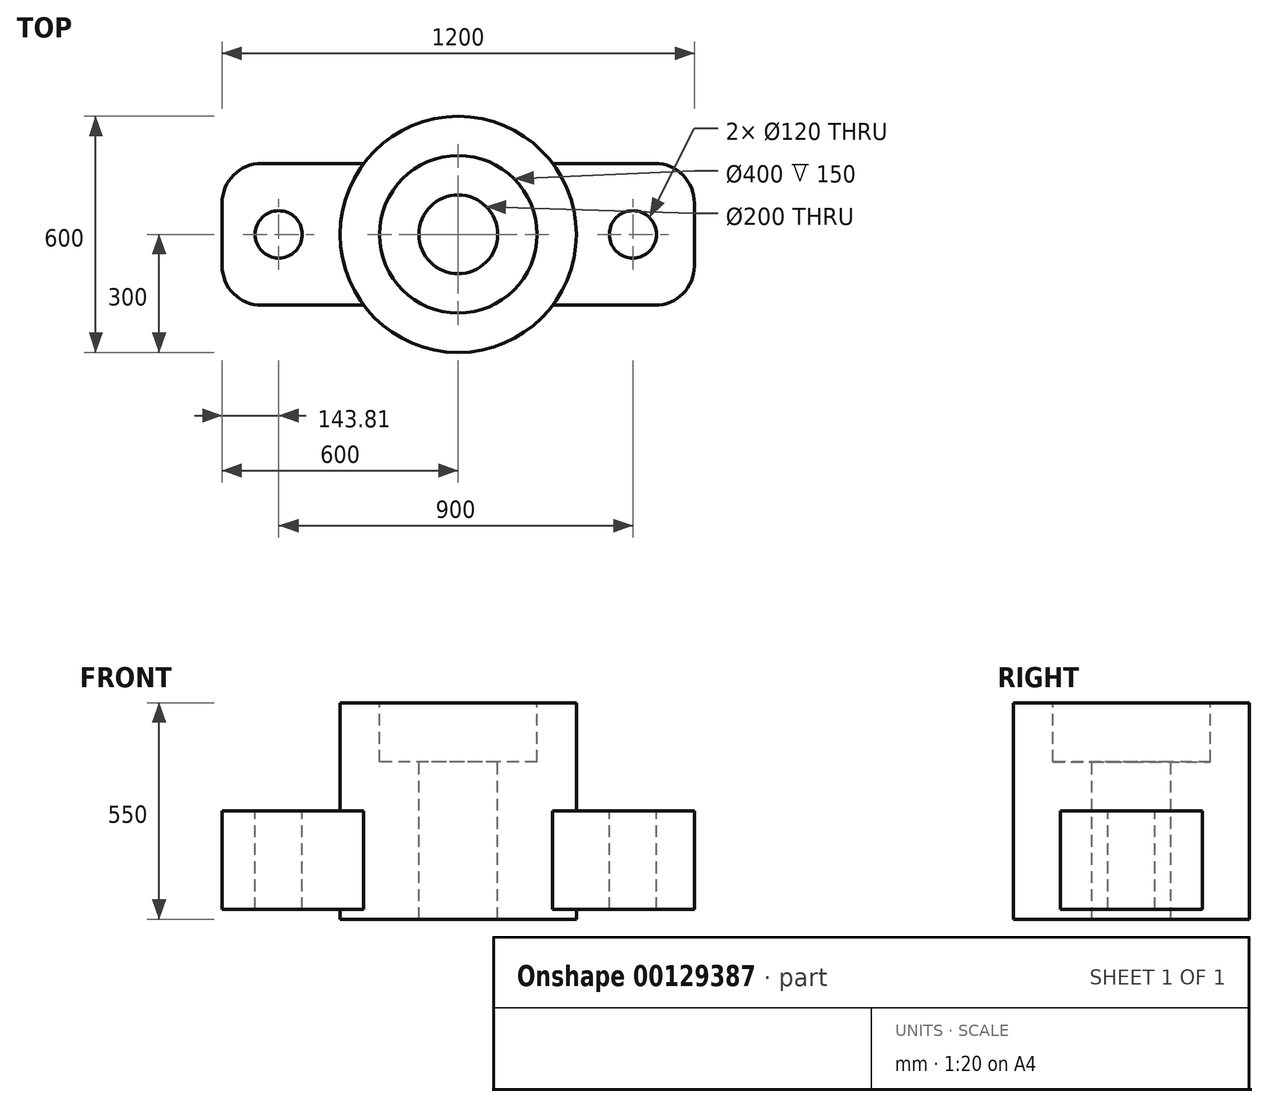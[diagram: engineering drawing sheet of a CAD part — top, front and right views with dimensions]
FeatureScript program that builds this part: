
annotation { "Feature Type Name" : "Feature", "Feature Type Description" : "" }
export const myFeature = defineFeature(function(context is Context, id is Id, definition is map)
    precondition{}
    {
        {
            var Q0;
            Q0=qCreatedBy(makeId("Top.planeOp"),FACE);
            var sketch = newSketch(context, id + "F0", { "sketchPlane" : qUnion([Q0])});
            skLineSegment(sketch, "E0.bottom", {"start": v(600, 180) * mm, "end": v(-600, 180) * mm});
            skLineSegment(sketch, "E0.top", {"start": v(600, -180) * mm, "end": v(-600, -180) * mm});
            skLineSegment(sketch, "E0.left", {"start": v(600, 180) * mm, "end": v(600, -180) * mm});
            skLineSegment(sketch, "E0.right", {"start": v(-600, 180) * mm, "end": v(-600, -180) * mm});
            skPoint(sketch, "E0.middle", {"position": v(0, 0) * mm});
            skSolve(sketch);
        }
        {
            var Q0;
            Q0=makeQuery(id+"F0.imprint","IMPRINT",FACE,{"disambiguationData":[TD([[makeQuery(id+"F0.imprint","IMPRINT",EDGE,{"derivedFrom":sQuery(id+"F0.wireOp",EDGE,"E0.bottom")}),1.0]])]});
            extrude(context, id + "F1", {"entities" : qUnion([Q0]), "depth" : 250 * mm});
        }
        {
            var Q0;
            Q0=makeQuery(id+"F1.opExtrude","CAP_FACE",FACE,{"disambiguationData":[OSD([sQuery(id+"F0.wireOp",EDGE,"E0.bottom"),sQuery(id+"F0.wireOp",EDGE,"E0.top"),sQuery(id+"F0.wireOp",EDGE,"E0.left"),sQuery(id+"F0.wireOp",EDGE,"E0.right")])],"isStart":false});
            var sketch = newSketch(context, id + "F2", { "sketchPlane" : qUnion([Q0])});
            skCircle(sketch, "E1", {"center": v(-456.2, 0) * mm, "radius": 60 * mm});
            skCircle(sketch, "E2", {"center": v(443.8, 0) * mm, "radius": 60 * mm});
            skSolve(sketch);
        }
        {
            var Q0;
            Q0=makeQuery(id+"F2.imprint","IMPRINT",FACE,{"disambiguationData":[TD([[makeQuery(id+"F2.imprint","IMPRINT",EDGE,{"derivedFrom":sQuery(id+"F2.wireOp",EDGE,"E1")}),1.0]])]});
            var Q1;
            Q1=makeQuery(id+"F2.imprint","IMPRINT",FACE,{"disambiguationData":[TD([[makeQuery(id+"F2.imprint","IMPRINT",EDGE,{"derivedFrom":sQuery(id+"F2.wireOp",EDGE,"E2")}),1.0]])]});
            extrude(context, id + "F3", {"entities" : qUnion([Q0, Q1]), "operationType" : NewBodyOperationType.REMOVE, "endBound" : BoundingType.THROUGH_ALL, "oppositeDirection" : true, "depth" : 25 * mm});
        }
        {
            var Q0;
            Q0=makeQuery(id+"F1.opExtrude","CAP_FACE",FACE,{"disambiguationData":[OSD([sQuery(id+"F0.wireOp",EDGE,"E0.bottom"),sQuery(id+"F0.wireOp",EDGE,"E0.top"),sQuery(id+"F0.wireOp",EDGE,"E0.left"),sQuery(id+"F0.wireOp",EDGE,"E0.right")])],"isStart":false});
            var sketch = newSketch(context, id + "F4", { "sketchPlane" : qUnion([Q0])});
            skCircle(sketch, "E3", {"center": v(0, 0) * mm, "radius": 300 * mm});
            skSolve(sketch);
        }
        {
            var Q0;
            Q0 = qSketchRegion(id + "F4", true);
            var Q1;
            {var subQ0=sQuery(id+"F4.wireOp",EDGE,"E3");var subQ1=makeQuery(id+"F1.opExtrude","CAP_EDGE",EDGE,{"disambiguationData":[OSD([sQuery(id+"F0.wireOp",EDGE,"E0.bottom")])],"isStart":false});var subQ2=makeQuery(id+"F4.imprint","INTERSECT",VERTEX,{"disambiguationData":[OD(0.0)],"derivedFrom":[subQ1,subQ0]});Q1=makeQuery(id+"F4.imprint","IMPRINT",FACE,{"disambiguationData":[TD([[makeQuery(id+"F4.imprint","IMPRINT",EDGE,{"disambiguationData":[TD([[subQ2,-1.0]])],"derivedFrom":subQ0}),1.0]])]});}
            extrude(context, id + "F5", {"entities" : qUnion([Q0, Q1]), "operationType" : NewBodyOperationType.ADD, "endBound" : BoundingType.SYMMETRIC, "depth" : 550 * mm});
        }
        {
            var Q0;
            Q0=makeQuery(id+"F5.opExtrude","CAP_FACE",FACE,{"disambiguationData":[OSD([sQuery(id+"F4.wireOp",EDGE,"E3")])],"isStart":false});
            var sketch = newSketch(context, id + "F6", { "sketchPlane" : qUnion([Q0])});
            skCircle(sketch, "E4", {"center": v(0, 0) * mm, "radius": 200 * mm});
            skSolve(sketch);
        }
        {
            var Q0;
            Q0=makeQuery(id+"F6.imprint","IMPRINT",FACE,{"disambiguationData":[TD([[makeQuery(id+"F6.imprint","IMPRINT",EDGE,{"derivedFrom":sQuery(id+"F6.wireOp",EDGE,"E4")}),1.0]])]});
            extrude(context, id + "F7", {"entities" : qUnion([Q0]), "operationType" : NewBodyOperationType.REMOVE, "oppositeDirection" : true, "depth" : 150 * mm});
        }
        {
            var Q0;
            Q0=makeQuery(id+"F7.boolean.opBoolean","COPY",FACE,{"derivedFrom":makeQuery(id+"F7.opExtrude","CAP_FACE",FACE,{"disambiguationData":[OSD([sQuery(id+"F6.wireOp",EDGE,"E4")])],"isStart":false})});
            var sketch = newSketch(context, id + "F8", { "sketchPlane" : qUnion([Q0])});
            skCircle(sketch, "E5", {"center": v(0, 0) * mm, "radius": 100 * mm});
            skSolve(sketch);
        }
        {
            var Q0;
            Q0=makeQuery(id+"F8.imprint","IMPRINT",FACE,{"disambiguationData":[TD([[makeQuery(id+"F8.imprint","IMPRINT",EDGE,{"derivedFrom":sQuery(id+"F8.wireOp",EDGE,"E5")}),1.0]])]});
            extrude(context, id + "F9", {"entities" : qUnion([Q0]), "operationType" : NewBodyOperationType.REMOVE, "endBound" : BoundingType.THROUGH_ALL, "oppositeDirection" : true, "depth" : 25 * mm});
        }
        {
            var Q0;
            Q0=makeQuery(id+"F1.opExtrude","SWEPT_EDGE",EDGE,{"disambiguationData":[OSD([sQuery(id+"F0.wireOp",EDGE,"E0.top"),sQuery(id+"F0.wireOp",EDGE,"E0.left")])]});
            var Q1;
            Q1=makeQuery(id+"F1.opExtrude","SWEPT_EDGE",EDGE,{"disambiguationData":[OSD([sQuery(id+"F0.wireOp",EDGE,"E0.bottom"),sQuery(id+"F0.wireOp",EDGE,"E0.left")])]});
            var Q2;
            Q2=makeQuery(id+"F1.opExtrude","SWEPT_EDGE",EDGE,{"disambiguationData":[OSD([sQuery(id+"F0.wireOp",EDGE,"E0.top"),sQuery(id+"F0.wireOp",EDGE,"E0.right")])]});
            var Q3;
            Q3=makeQuery(id+"F1.opExtrude","SWEPT_EDGE",EDGE,{"disambiguationData":[OSD([sQuery(id+"F0.wireOp",EDGE,"E0.bottom"),sQuery(id+"F0.wireOp",EDGE,"E0.right")])]});
            fillet(context, id + "F10", {"entities" : qUnion([Q0, Q1, Q2, Q3]), "radius" : 100 * mm, "tangentPropagation" : true, "allowEdgeOverflow" : false});
        }
    });
